# Revit family: 1Electronics_Community-Point-Source_Biamp_Loudspeaker_IP8_1153
name_source: partatom
category: Communication Devices
units: mm (PartAtom-declared; Revit-internal decimal feet)

## family parameters
Cut with Voids When Loaded = No
Host = Face
Maintain Annotation Orientation = No
OmniClass Number = 23.85.10.11.14.14.14
Part Type = Normal
Room Calculation Point = No
Round Connector Dimension = Use Diameter
Shared = No

## types (1)
- Please download type catalogue!
    Continuous Power Handling  Nominal Impedance = LF - 69V, 600W @ 8 ohms (2400W peak); MF - 35V, 150W @ 8 ohms (600W peak); HF - 32V, 125W @ 8 ohms (500W peak); MF/HF - 47V, 275W @ 8 ohms (1100W peak)
    Default Elevation = 4' - 0"
    Depth = 2' - 2 5/16"
    Description = IP8-1153 High Power 15-Inch Three-Way Installation Loudspeaker
    Environmental = MIL-STD-810G
    Equalized Maximum SPL = Peak: 127 dB - Continuous: 121 dB
    Equalized Sensitivity = 1W: 93 dB - 2.83V: 93 dB
    Gril Material = Biamp - Plastic - Black(Grid)
    Height = 3' - 3"
    Housing Material = Biamp - Plastic - Black
    Input Connection = Screw terminal blocks (6-position)
    Manufacturer = Biamp
    Mounting Points = 15
    Operating Environment = Indoor
    Operating Mode = Biamp or Triamp with DSP
    Product Documentation Link = https://www.biamp.com
    Product Page URL = https://www.biamp.com
    Product data url = https://www.bimobject.com
    Recommended Amplifiers = LF - 600W - 1200W @ 8 ohms, (69V - 98V); MF - 150W - 300W @ 8 ohms (35V - 49V); HF - 125W - 250W @ 8 ohms (32V - 45V); MF/HF - 275W - 550W @ 8 ohms (47V - 66V)
    Shipping Weight = 124.00 lbf
    Transducers = LF – 1 x 15 (381mm) neodymium motor woofer, 3 (76mm) voice coil, demodulation ring; MF - M200HP, 2 exit, ketone polymer diaphragm, compression driver; HF – 1 x 1.4 (36mm) exit neodymium compression driver, 2.6 (66mm) voice coil, demodulation ring, ketone polymer diaphragm
    URL = https://www.biamp.com
    Weight = 105.00 lbf
    Width = 1' - 10 3/32"

## geometry (parser evidence)
native form markers: Sweep x2
no freeform markers — native parametric forms only
